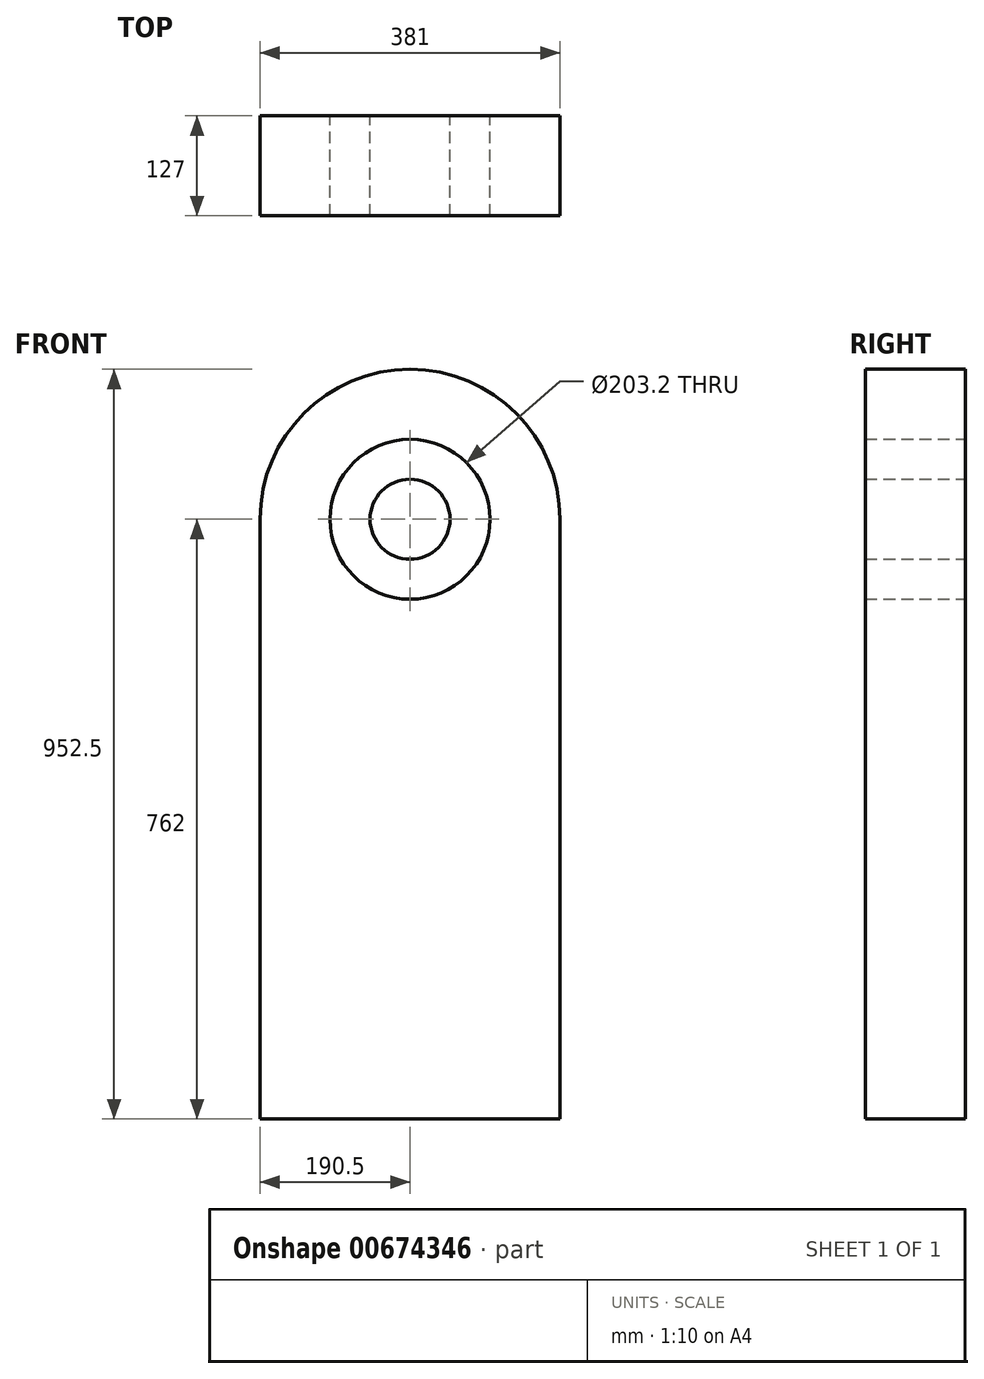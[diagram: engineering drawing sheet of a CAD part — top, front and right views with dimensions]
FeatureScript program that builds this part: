
annotation { "Feature Type Name" : "Feature", "Feature Type Description" : "" }
export const myFeature = defineFeature(function(context is Context, id is Id, definition is map)
    precondition{}
    {
        {
            var Q0;
            Q0=qCreatedBy(makeId("Front.planeOp"),FACE);
            var sketch = newSketch(context, id + "F0", { "sketchPlane" : qUnion([Q0])});
            skLineSegment(sketch, "E0.bottom", {"start": v(0, 0) * mm, "end": v(381, 0) * mm});
            skLineSegment(sketch, "E0.left", {"start": v(0, 0) * mm, "end": v(0, 762) * mm});
            skLineSegment(sketch, "E0.right", {"start": v(381, 0) * mm, "end": v(381, 762) * mm});
            skArc(sketch, "E1", {"start": v(0, 762) * mm, "mid": v(190.5, 952.5) * mm, "end": v(381, 762) * mm});
            skCircle(sketch, "E2", {"center": v(190.5, 762) * mm, "radius": 101.6 * mm});
            skCircle(sketch, "E3", {"center": v(190.5, 762) * mm, "radius": 50.8 * mm});
            skSolve(sketch);
        }
        {
            var Q0;
            Q0=makeQuery(id+"F0.imprint","IMPRINT",FACE,{"disambiguationData":[TD([[makeQuery(id+"F0.imprint","IMPRINT",EDGE,{"derivedFrom":sQuery(id+"F0.wireOp",EDGE,"E0.bottom")}),1.0]])]});
            var Q1;
            Q1=makeQuery(id+"F0.imprint","IMPRINT",FACE,{"disambiguationData":[TD([[makeQuery(id+"F0.imprint","IMPRINT",EDGE,{"derivedFrom":sQuery(id+"F0.wireOp",EDGE,"E3")}),1.0]])]});
            extrude(context, id + "F1", {"entities" : qUnion([Q0, Q1]), "depth" : 127 * mm, "offsetDistance" : 25.4 * mm});
        }
    });
